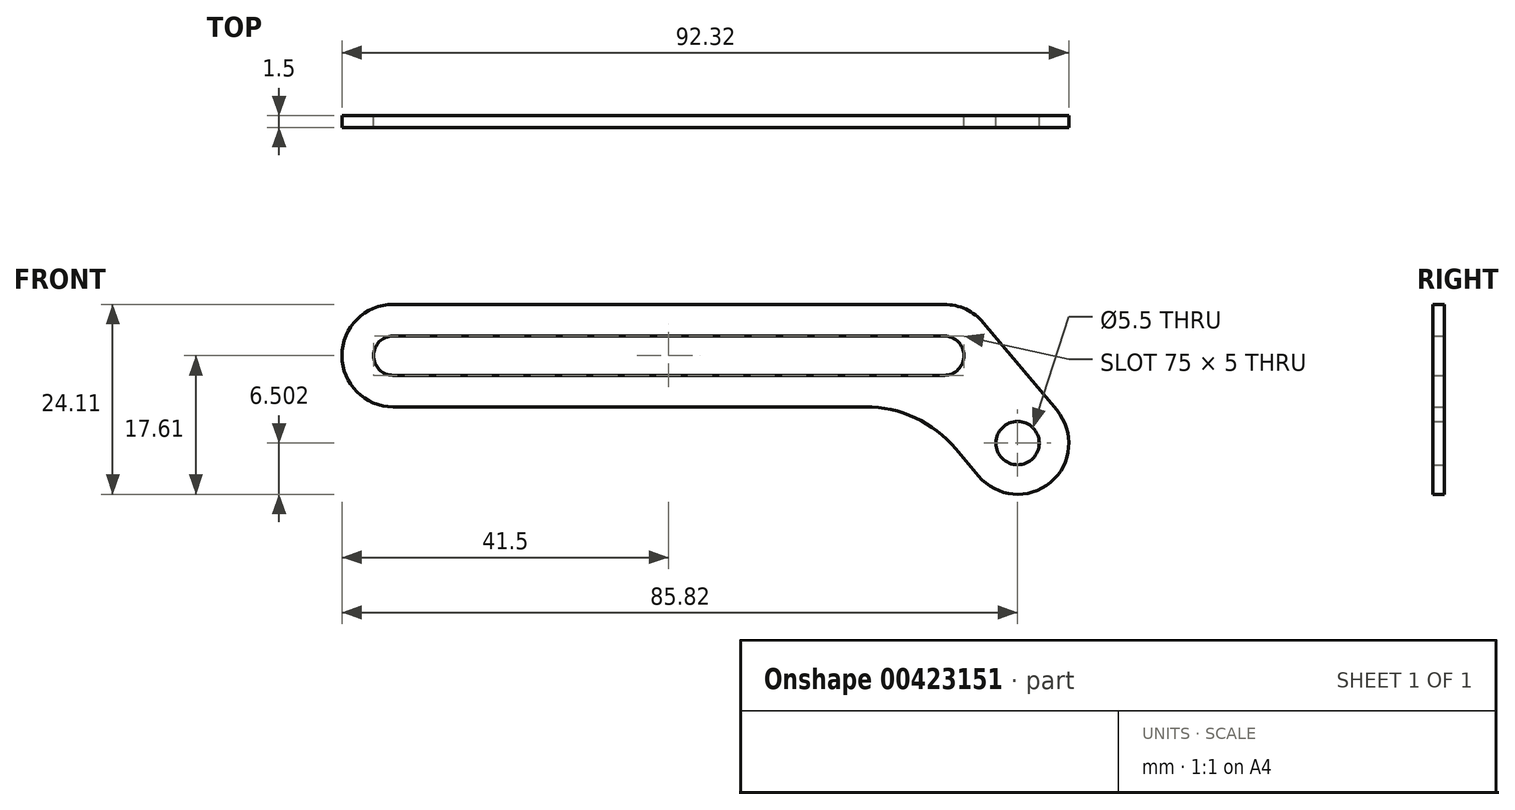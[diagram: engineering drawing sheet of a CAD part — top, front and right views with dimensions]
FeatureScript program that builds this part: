
annotation { "Feature Type Name" : "Feature", "Feature Type Description" : "" }
export const myFeature = defineFeature(function(context is Context, id is Id, definition is map)
    precondition{}
    {
        {
            var Q0;
            Q0=qCreatedBy(makeId("Front.planeOp"),FACE);
            var sketch = newSketch(context, id + "F0", { "sketchPlane" : qUnion([Q0])});
            skLineSegment(sketch, "E0", {"start": v(0, 0) * mm, "end": v(-70, 0) * mm, "construction": true});
            skArc(sketch, "E1.0.startCap", {"start": v(0, 6.5) * mm, "mid": v(2.75, 5.9) * mm, "end": v(4.98, 4.18) * mm});
            skArc(sketch, "E1.0.endCap", {"start": v(-70, -6.5) * mm, "mid": v(-76.5, 0) * mm, "end": v(-70, 6.5) * mm});
            skLineSegment(sketch, "E1.0.left", {"start": v(-3.03, -6.5) * mm, "end": v(-70, -6.5) * mm});
            skLineSegment(sketch, "E1.0.right", {"start": v(0, 6.5) * mm, "end": v(-70, 6.5) * mm});
            skArc(sketch, "E2.0.startCap", {"start": v(0, 2.5) * mm, "mid": v(2.5, 0) * mm, "end": v(0, -2.5) * mm});
            skArc(sketch, "E2.0.endCap", {"start": v(-70, -2.5) * mm, "mid": v(-72.5, 0) * mm, "end": v(-70, 2.5) * mm});
            skLineSegment(sketch, "E2.0.left", {"start": v(0, -2.5) * mm, "end": v(-70, -2.5) * mm});
            skLineSegment(sketch, "E2.0.right", {"start": v(0, 2.5) * mm, "end": v(-70, 2.5) * mm});
            skLineSegment(sketch, "E3", {"start": v(0, 0) * mm, "end": v(9.32, -11.1) * mm, "construction": true});
            skLineSegment(sketch, "E4", {"start": v(0, 0) * mm, "end": v(0, -28.2) * mm, "construction": true});
            skArc(sketch, "E5.0.endCap", {"start": v(14.3, -6.93) * mm, "mid": v(13.5, -16.09) * mm, "end": v(4.34, -15.29) * mm});
            skLineSegment(sketch, "E5.0.left", {"start": v(4.98, 4.18) * mm, "end": v(14.3, -6.93) * mm});
            skLineSegment(sketch, "E5.0.right", {"start": v(-3.03, -6.5) * mm, "end": v(4.34, -15.29) * mm});
            skCircle(sketch, "E6", {"center": v(9.32, -11.1) * mm, "radius": 2.75 * mm});
            skSolve(sketch);
        }
        {
            var Q0;
            Q0 = qSketchRegion(id + "F0", true);
            extrude(context, id + "F1", {"entities" : qUnion([Q0]), "depth" : 1.5 * mm});
        }
        {
            var Q0;
            Q0=makeQuery(id+"F1.opExtrude","SWEPT_EDGE",EDGE,{"disambiguationData":[OSD([sQuery(id+"F0.wireOp",EDGE,"E1.0.left"),sQuery(id+"F0.wireOp",EDGE,"E5.0.right")])]});
            fillet(context, id + "F2", {"entities" : qUnion([Q0]), "radius" : 15 * mm, "tangentPropagation" : true, "allowEdgeOverflow" : false});
        }
    });
